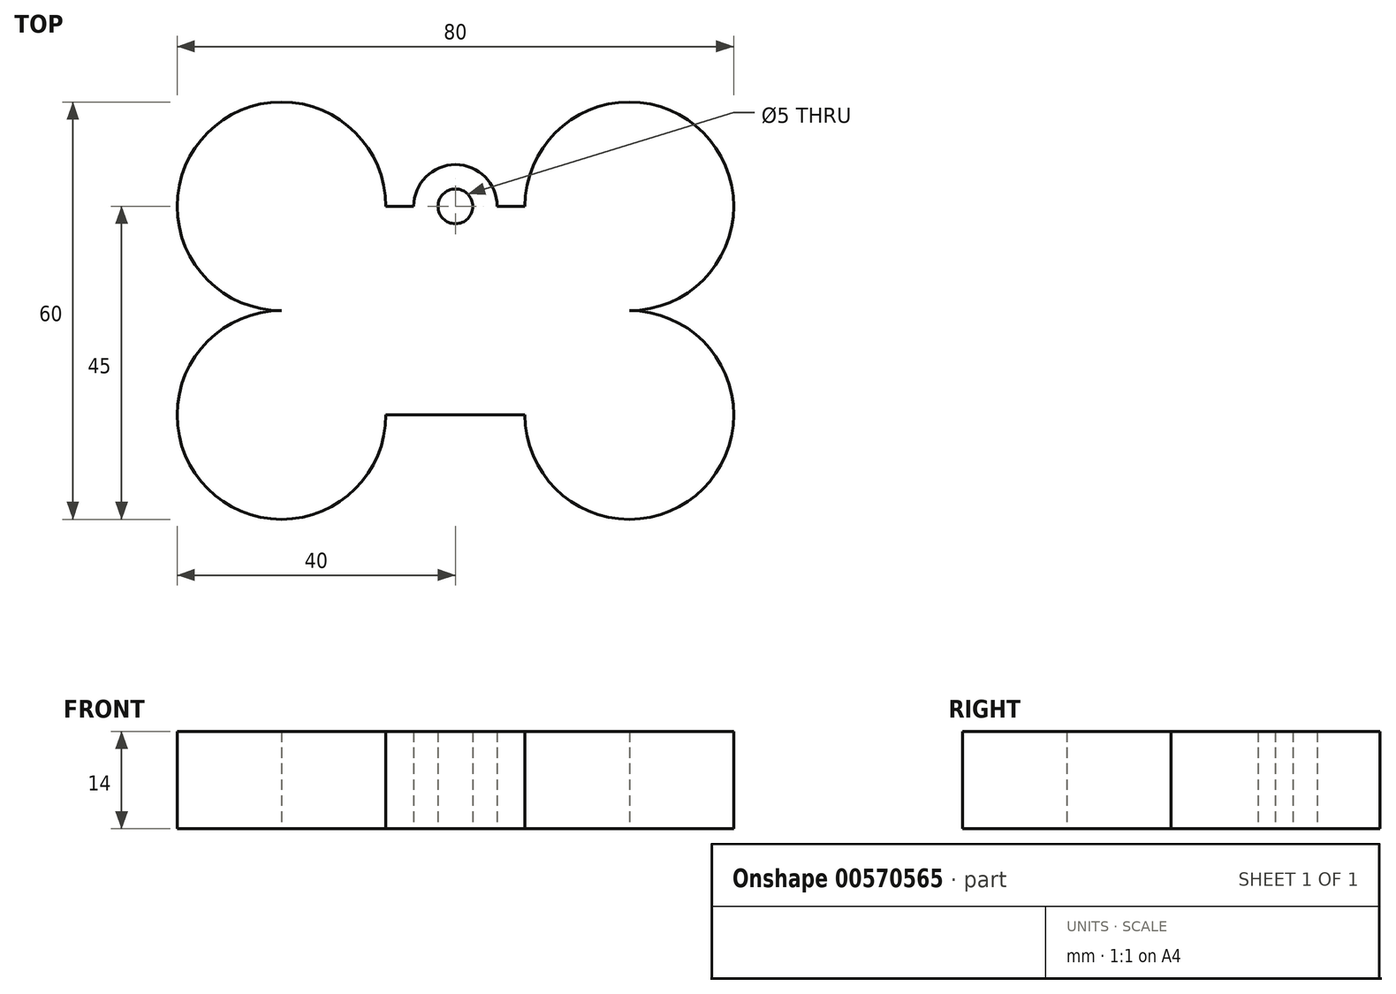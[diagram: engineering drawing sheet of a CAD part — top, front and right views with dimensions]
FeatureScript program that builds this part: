
annotation { "Feature Type Name" : "Feature", "Feature Type Description" : "" }
export const myFeature = defineFeature(function(context is Context, id is Id, definition is map)
    precondition{}
    {
        {
            var Q0;
            Q0=qCreatedBy(makeId("Top.planeOp"),FACE);
            var sketch = newSketch(context, id + "F0", { "sketchPlane" : qUnion([Q0])});
            skLineSegment(sketch, "E0.bottom", {"start": v(-10, 15) * mm, "end": v(-6, 15) * mm});
            skLineSegment(sketch, "E0.top", {"start": v(-10, -15) * mm, "end": v(10, -15) * mm});
            skPoint(sketch, "E0.middle", {"position": v(0, 0) * mm});
            skArc(sketch, "E1", {"start": v(25, 0) * mm, "mid": v(35.6, 25.6) * mm, "end": v(10, 15) * mm});
            skArc(sketch, "E2", {"start": v(-10, 15) * mm, "mid": v(-35.6, 25.6) * mm, "end": v(-25, 0) * mm});
            skArc(sketch, "E3", {"start": v(-25, 0) * mm, "mid": v(-35.6, -25.6) * mm, "end": v(-10, -15) * mm});
            skArc(sketch, "E4", {"start": v(10, -15) * mm, "mid": v(35.6, -25.6) * mm, "end": v(25, 0) * mm});
            skArc(sketch, "E5", {"start": v(6, 15) * mm, "mid": v(0, 21) * mm, "end": v(-6, 15) * mm});
            skCircle(sketch, "E6", {"center": v(0, 15) * mm, "radius": 2.5 * mm});
            skLineSegment(sketch, "E7.trimOffspring", {"start": v(6, 15) * mm, "end": v(10, 15) * mm});
            skLineSegment(sketch, "E8.trimOffspring", {"start": v(-2.5, 15) * mm, "end": v(2.5, 15) * mm});
            skSolve(sketch);
        }
        {
            var Q0;
            Q0=makeQuery(id+"F0.imprint","IMPRINT",FACE,{"disambiguationData":[TD([[makeQuery(id+"F0.imprint","IMPRINT",EDGE,{"derivedFrom":sQuery(id+"F0.wireOp",EDGE,"E0.bottom")}),-1.0]])]});
            extrude(context, id + "F1", {"entities" : qUnion([Q0]), "depth" : 4 * mm, "offsetDistance" : 25 * mm});
        }
        {
            var Q0;
            Q0=makeQuery(id+"F1.opExtrude","CAP_FACE",FACE,{"disambiguationData":[OSD([sQuery(id+"F0.wireOp",EDGE,"E0.bottom"),sQuery(id+"F0.wireOp",EDGE,"E0.top"),sQuery(id+"F0.wireOp",EDGE,"E1"),sQuery(id+"F0.wireOp",EDGE,"E2"),sQuery(id+"F0.wireOp",EDGE,"E3"),sQuery(id+"F0.wireOp",EDGE,"E4"),sQuery(id+"F0.wireOp",EDGE,"E5"),sQuery(id+"F0.wireOp",EDGE,"E6"),sQuery(id+"F0.wireOp",EDGE,"E7.trimOffspring")])],"isStart":false});
            extrude(context, id + "F2", {"entities" : qUnion([Q0]), "operationType" : NewBodyOperationType.ADD, "depth" : 10 * mm, "offsetDistance" : 25 * mm});
        }
    });
